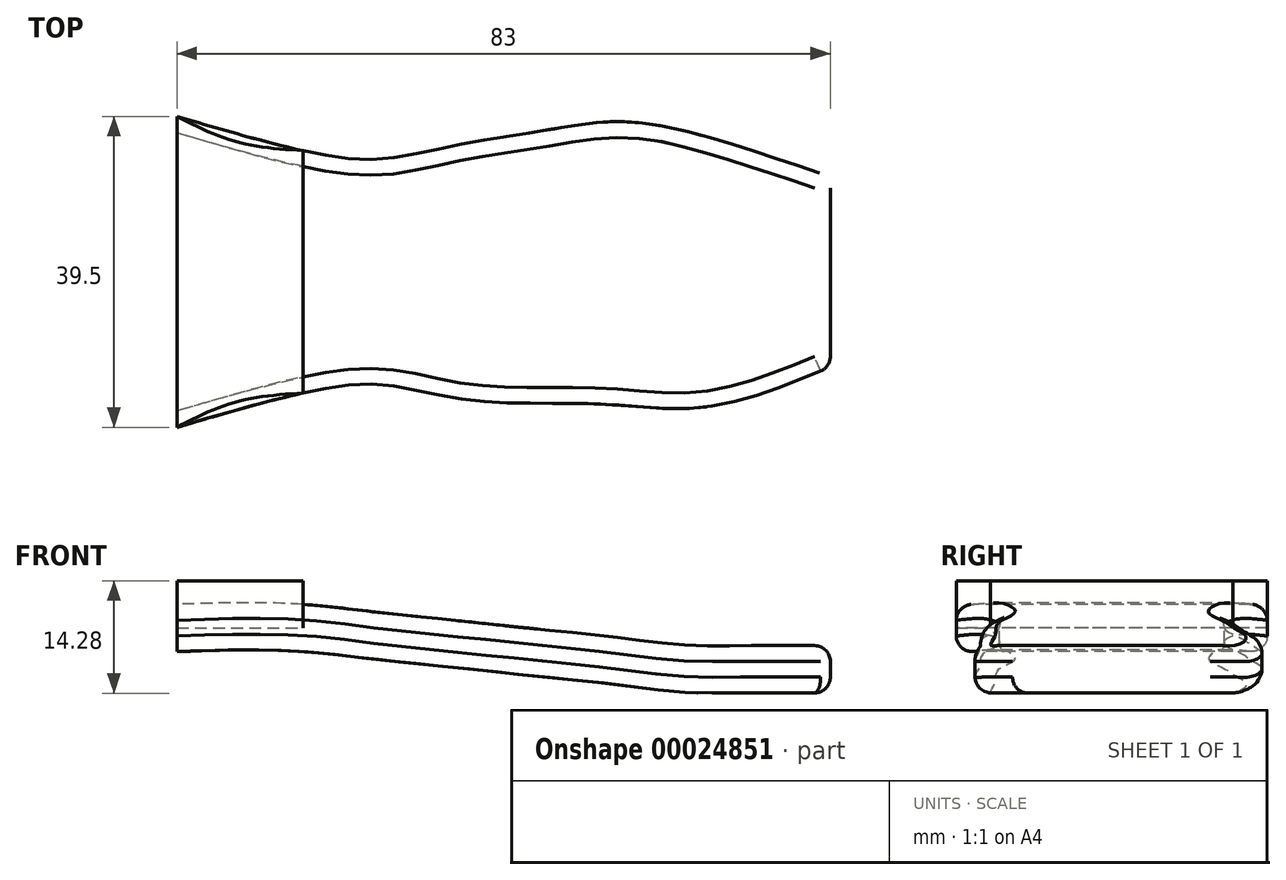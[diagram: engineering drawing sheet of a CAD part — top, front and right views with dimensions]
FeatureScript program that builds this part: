
annotation { "Feature Type Name" : "Feature", "Feature Type Description" : "" }
export const myFeature = defineFeature(function(context is Context, id is Id, definition is map)
    precondition{}
    {
        {
            var Q0;
            Q0=qCreatedBy(makeId("Top.planeOp"),FACE);
            var sketch = newSketch(context, id + "F0", { "sketchPlane" : qUnion([Q0])});
            skFitSpline(sketch, "E0", {"points": [v(0, 19.75) * mm, v(7.58, 16.5) * mm, v(16, 15.4) * mm], "startDerivative": vector(14.91, -7.63) * mm, "endDerivative": vector(17.08, -1.1) * mm});
            skFitSpline(sketch, "E1.MirrorCS", {"points": [v(0, -19.75) * mm, v(7.58, -16.5) * mm, v(16, -15.4) * mm], "startDerivative": vector(14.91, 7.63) * mm, "endDerivative": vector(17.08, 1.1) * mm});
            skLineSegment(sketch, "E2", {"start": v(0, 19.75) * mm, "end": v(0, -19.75) * mm});
            skLineSegment(sketch, "E3", {"start": v(16, 15.4) * mm, "end": v(16, -15.4) * mm});
            skSolve(sketch);
        }
        {
            var Q0;
            Q0=makeQuery(id+"F0.imprint","IMPRINT",FACE,{"disambiguationData":[TD([[makeQuery(id+"F0.imprint","IMPRINT",EDGE,{"derivedFrom":sQuery(id+"F0.wireOp",EDGE,"E0")}),-1.0]])]});
            extrude(context, id + "F1", {"entities" : qUnion([Q0]), "depth" : 6 * mm});
        }
        {
            var Q0;
            Q0=makeQuery(id+"F1.opExtrude","SWEPT_FACE",FACE,{"disambiguationData":[OSD([sQuery(id+"F0.wireOp",EDGE,"E3")])]});
            cPlane(context, id + "F2", {"entities" : qUnion([Q0]), "cplaneType" : CPlaneType.OFFSET, "offset" : 0 * mm, "width" : 152.4 * mm, "height" : 152.4 * mm});
        }
        {
            var Q0;
            Q0=qCreatedBy(id+"F2.planeOp",FACE);
            cPlane(context, id + "F3", {"entities" : qUnion([Q0]), "cplaneType" : CPlaneType.OFFSET, "offset" : 9.5 * mm, "width" : 152.4 * mm, "height" : 152.4 * mm});
        }
        {
            var Q0;
            Q0=qCreatedBy(id+"F3.planeOp",FACE);
            cPlane(context, id + "F4", {"entities" : qUnion([Q0]), "cplaneType" : CPlaneType.OFFSET, "offset" : 9.5 * mm, "width" : 152.4 * mm, "height" : 152.4 * mm});
        }
        {
            var Q0;
            Q0=qCreatedBy(id+"F3.planeOp",FACE);
            var sketch = newSketch(context, id + "F5", { "sketchPlane" : qUnion([Q0])});
            skLineSegment(sketch, "E4.rect.bottom", {"start": v(-14.3, 2) * mm, "end": v(14.3, 2) * mm});
            skLineSegment(sketch, "E4.rect.top", {"start": v(-14.3, -4) * mm, "end": v(14.3, -4) * mm});
            skLineSegment(sketch, "E4.rect.left", {"start": v(-14.3, 2) * mm, "end": v(-14.3, -4) * mm});
            skLineSegment(sketch, "E4.rect.right", {"start": v(14.3, 2) * mm, "end": v(14.3, -4) * mm});
            skPoint(sketch, "E4.rect.middle", {"position": v(0, -1) * mm});
            skSolve(sketch);
        }
        {
            var Q0;
            Q0=qCreatedBy(id+"F4.planeOp",FACE);
            var sketch = newSketch(context, id + "F6", { "sketchPlane" : qUnion([Q0])});
            skLineSegment(sketch, "E5.rect.bottom", {"start": v(16, 1) * mm, "end": v(-16, 1) * mm});
            skLineSegment(sketch, "E5.rect.top", {"start": v(16, -5) * mm, "end": v(-16, -5) * mm});
            skLineSegment(sketch, "E5.rect.left", {"start": v(16, 1) * mm, "end": v(16, -5) * mm});
            skLineSegment(sketch, "E5.rect.right", {"start": v(-16, 1) * mm, "end": v(-16, -5) * mm});
            skSolve(sketch);
        }
        {
            var Q0;
            Q0=qCreatedBy(id+"F4.planeOp",FACE);
            cPlane(context, id + "F7", {"entities" : qUnion([Q0]), "cplaneType" : CPlaneType.OFFSET, "offset" : 12 * mm, "width" : 152.4 * mm, "height" : 152.4 * mm});
        }
        {
            var Q0;
            Q0=qCreatedBy(id+"F7.planeOp",FACE);
            cPlane(context, id + "F8", {"entities" : qUnion([Q0]), "cplaneType" : CPlaneType.OFFSET, "offset" : 8.5 * mm, "width" : 152.4 * mm, "height" : 152.4 * mm});
        }
        {
            var Q0;
            Q0=qCreatedBy(id+"F8.planeOp",FACE);
            cPlane(context, id + "F9", {"entities" : qUnion([Q0]), "cplaneType" : CPlaneType.OFFSET, "offset" : 10.5 * mm, "width" : 152.4 * mm, "height" : 152.4 * mm});
        }
        {
            var Q0;
            Q0=qCreatedBy(id+"F9.planeOp",FACE);
            cPlane(context, id + "F10", {"entities" : qUnion([Q0]), "cplaneType" : CPlaneType.OFFSET, "offset" : 4 * mm, "width" : 152.4 * mm, "height" : 152.4 * mm});
        }
        {
            var Q0;
            Q0=qCreatedBy(id+"F10.planeOp",FACE);
            cPlane(context, id + "F11", {"entities" : qUnion([Q0]), "cplaneType" : CPlaneType.OFFSET, "offset" : 13 * mm, "width" : 152.4 * mm, "height" : 152.4 * mm});
        }
        {
            var Q0;
            Q0=qCreatedBy(id+"F7.planeOp",FACE);
            var sketch = newSketch(context, id + "F12", { "sketchPlane" : qUnion([Q0])});
            skPoint(sketch, "E6.rect.middle", {"position": v(0, -3.26) * mm});
            skLineSegment(sketch, "E7", {"start": v(-16.7, -0.26) * mm, "end": v(18, -0.26) * mm});
            skLineSegment(sketch, "E8.MirrorCS", {"start": v(-16.7, -6.26) * mm, "end": v(18, -6.26) * mm});
            skLineSegment(sketch, "E9", {"start": v(-16.7, -0.26) * mm, "end": v(-16.7, -6.26) * mm});
            skLineSegment(sketch, "E10", {"start": v(18, -0.26) * mm, "end": v(18, -6.26) * mm});
            skSolve(sketch);
        }
        {
            var Q0;
            Q0=qCreatedBy(id+"F8.planeOp",FACE);
            var sketch = newSketch(context, id + "F13", { "sketchPlane" : qUnion([Q0])});
            skLineSegment(sketch, "E11", {"start": v(19.08, -1.15) * mm, "end": v(-16.9, -1.15) * mm});
            skLineSegment(sketch, "E12.MirrorCS", {"start": v(19.08, -7.15) * mm, "end": v(-16.9, -7.15) * mm});
            skLineSegment(sketch, "E13", {"start": v(-16.9, -7.15) * mm, "end": v(-16.9, -1.15) * mm});
            skLineSegment(sketch, "E14", {"start": v(19.08, -1.15) * mm, "end": v(19.08, -7.15) * mm});
            skSolve(sketch);
        }
        {
            var Q0;
            Q0=qCreatedBy(id+"F9.planeOp",FACE);
            var sketch = newSketch(context, id + "F14", { "sketchPlane" : qUnion([Q0])});
            skLineSegment(sketch, "E15", {"start": v(-17.3, -2.25) * mm, "end": v(17.5, -2.25) * mm});
            skLineSegment(sketch, "E16.MirrorCS", {"start": v(-17.3, -8.25) * mm, "end": v(17.5, -8.25) * mm});
            skLineSegment(sketch, "E17", {"start": v(17.5, -2.25) * mm, "end": v(17.5, -8.25) * mm});
            skLineSegment(sketch, "E18", {"start": v(-17.3, -2.25) * mm, "end": v(-17.3, -8.25) * mm});
            skSolve(sketch);
        }
        {
            var Q0;
            Q0=qCreatedBy(id+"F10.planeOp",FACE);
            var sketch = newSketch(context, id + "F15", { "sketchPlane" : qUnion([Q0])});
            skLineSegment(sketch, "E19", {"start": v(-16.68, -2.25) * mm, "end": v(16.35, -2.25) * mm});
            skLineSegment(sketch, "E20.MirrorCS", {"start": v(-16.68, -8.25) * mm, "end": v(16.35, -8.25) * mm});
            skLineSegment(sketch, "E21", {"start": v(16.35, -2.25) * mm, "end": v(16.35, -8.25) * mm});
            skLineSegment(sketch, "E22", {"start": v(-16.68, -2.25) * mm, "end": v(-16.68, -8.25) * mm});
            skSolve(sketch);
        }
        {
            var Q0;
            Q0=qCreatedBy(id+"F11.planeOp",FACE);
            var sketch = newSketch(context, id + "F16", { "sketchPlane" : qUnion([Q0])});
            skLineSegment(sketch, "E23.rect.bottom", {"start": v(-12.09, -2.25) * mm, "end": v(12.09, -2.25) * mm});
            skLineSegment(sketch, "E23.rect.top", {"start": v(-12.09, -8.25) * mm, "end": v(12.09, -8.25) * mm});
            skLineSegment(sketch, "E23.rect.left", {"start": v(-12.09, -2.25) * mm, "end": v(-12.09, -8.25) * mm});
            skLineSegment(sketch, "E23.rect.right", {"start": v(12.09, -2.25) * mm, "end": v(12.09, -8.25) * mm});
            skSolve(sketch);
        }
        {
            var Q0;
            Q0=qCreatedBy(makeId("Right.planeOp"),FACE);
            var sketch = newSketch(context, id + "F17", { "sketchPlane" : qUnion([Q0])});
            skLineSegment(sketch, "E24.rect.bottom", {"start": v(19.75, 3) * mm, "end": v(-19.75, 3) * mm});
            skLineSegment(sketch, "E24.rect.top", {"start": v(19.75, -3) * mm, "end": v(-19.75, -3) * mm});
            skLineSegment(sketch, "E24.rect.left", {"start": v(19.75, 3) * mm, "end": v(19.75, -3) * mm});
            skLineSegment(sketch, "E24.rect.right", {"start": v(-19.75, 3) * mm, "end": v(-19.75, -3) * mm});
            skPoint(sketch, "E24.rect.middle", {"position": v(0, 0) * mm});
            skSolve(sketch);
        }
        {
            var Q0;
            Q0=qCreatedBy(id+"F2.planeOp",FACE);
            var sketch = newSketch(context, id + "F18", { "sketchPlane" : qUnion([Q0])});
            skLineSegment(sketch, "E25.rect.bottom", {"start": v(-15.4, 3) * mm, "end": v(15.4, 3) * mm});
            skLineSegment(sketch, "E25.rect.top", {"start": v(-15.4, -3) * mm, "end": v(15.4, -3) * mm});
            skLineSegment(sketch, "E25.rect.left", {"start": v(-15.4, 3) * mm, "end": v(-15.4, -3) * mm});
            skLineSegment(sketch, "E25.rect.right", {"start": v(15.4, 3) * mm, "end": v(15.4, -3) * mm});
            skPoint(sketch, "E25.rect.middle", {"position": v(0, 0) * mm});
            skSolve(sketch);
        }
        {
            var Q0;
            Q0=makeQuery(id+"F17.imprint","IMPRINT",FACE,{"disambiguationData":[TD([[makeQuery(id+"F17.imprint","IMPRINT",EDGE,{"derivedFrom":sQuery(id+"F17.wireOp",EDGE,"E24.rect.bottom")}),1.0]])]});
            var Q1;
            Q1=makeQuery(id+"F18.imprint","IMPRINT",FACE,{"disambiguationData":[TD([[makeQuery(id+"F18.imprint","IMPRINT",EDGE,{"derivedFrom":sQuery(id+"F18.wireOp",EDGE,"E25.rect.bottom")}),-1.0]])]});
            var Q2;
            Q2=makeQuery(id+"F5.imprint","IMPRINT",FACE,{"disambiguationData":[TD([[makeQuery(id+"F5.imprint","IMPRINT",EDGE,{"derivedFrom":sQuery(id+"F5.wireOp",EDGE,"E4.rect.bottom")}),-1.0]])]});
            var Q3;
            Q3=makeQuery(id+"F6.imprint","IMPRINT",FACE,{"disambiguationData":[TD([[makeQuery(id+"F6.imprint","IMPRINT",EDGE,{"derivedFrom":sQuery(id+"F6.wireOp",EDGE,"E5.rect.bottom")}),1.0]])]});
            var Q4;
            Q4=makeQuery(id+"F12.imprint","IMPRINT",FACE,{"disambiguationData":[TD([[makeQuery(id+"F12.imprint","IMPRINT",EDGE,{"derivedFrom":sQuery(id+"F12.wireOp",EDGE,"E7")}),-1.0]])]});
            var Q5;
            Q5=makeQuery(id+"F13.imprint","IMPRINT",FACE,{"disambiguationData":[TD([[makeQuery(id+"F13.imprint","IMPRINT",EDGE,{"derivedFrom":sQuery(id+"F13.wireOp",EDGE,"E11")}),1.0]])]});
            var Q6;
            Q6=makeQuery(id+"F14.imprint","IMPRINT",FACE,{"disambiguationData":[TD([[makeQuery(id+"F14.imprint","IMPRINT",EDGE,{"derivedFrom":sQuery(id+"F14.wireOp",EDGE,"E15")}),-1.0]])]});
            var Q7;
            Q7=makeQuery(id+"F15.imprint","IMPRINT",FACE,{"disambiguationData":[TD([[makeQuery(id+"F15.imprint","IMPRINT",EDGE,{"derivedFrom":sQuery(id+"F15.wireOp",EDGE,"E19")}),-1.0]])]});
            var Q8;
            Q8=makeQuery(id+"F16.imprint","IMPRINT",FACE,{"disambiguationData":[TD([[makeQuery(id+"F16.imprint","IMPRINT",EDGE,{"derivedFrom":sQuery(id+"F16.wireOp",EDGE,"E23.rect.bottom")}),-1.0]])]});
            loft(context, id + "F19", {"sheetProfilesArray" : [{ "sheetProfileEntities" : qUnion([Q0]) }, { "sheetProfileEntities" : qUnion([Q1]) }, { "sheetProfileEntities" : qUnion([Q2]) }, { "sheetProfileEntities" : qUnion([Q3]) }, { "sheetProfileEntities" : qUnion([Q4]) }, { "sheetProfileEntities" : qUnion([Q5]) }, { "sheetProfileEntities" : qUnion([Q6]) }, { "sheetProfileEntities" : qUnion([Q7]) }, { "sheetProfileEntities" : qUnion([Q8]) }]});
        }
        {
            var Q0;
            Q0=makeQuery(id+"F19.opLoft","SWEPT_EDGE",EDGE,{"disambiguationData":[OSD([sQuery(id+"F17.wireOp",EDGE,"E24.rect.bottom"),sQuery(id+"F17.wireOp",EDGE,"E24.rect.right"),sQuery(id+"F18.wireOp",EDGE,"E25.rect.bottom"),sQuery(id+"F18.wireOp",EDGE,"E25.rect.left")])]});
            var Q1;
            Q1=makeQuery(id+"F19.opLoft","SWEPT_EDGE",EDGE,{"disambiguationData":[OSD([sQuery(id+"F17.wireOp",EDGE,"E24.rect.top"),sQuery(id+"F17.wireOp",EDGE,"E24.rect.right"),sQuery(id+"F18.wireOp",EDGE,"E25.rect.top"),sQuery(id+"F18.wireOp",EDGE,"E25.rect.left")])]});
            var Q2;
            Q2=makeQuery(id+"F19.opLoft","SWEPT_EDGE",EDGE,{"disambiguationData":[OSD([sQuery(id+"F15.wireOp",EDGE,"E19"),sQuery(id+"F15.wireOp",EDGE,"E21"),sQuery(id+"F16.wireOp",EDGE,"E23.rect.bottom"),sQuery(id+"F16.wireOp",EDGE,"E23.rect.right")])]});
            var Q3;
            Q3=makeQuery(id+"F19.opLoft","SWEPT_EDGE",EDGE,{"disambiguationData":[OSD([sQuery(id+"F15.wireOp",EDGE,"E20.MirrorCS"),sQuery(id+"F15.wireOp",EDGE,"E21"),sQuery(id+"F16.wireOp",EDGE,"E23.rect.top"),sQuery(id+"F16.wireOp",EDGE,"E23.rect.right")])]});
            var Q4;
            Q4=makeQuery(id+"F19.opLoft","MID_CAP_EDGE",EDGE,{"disambiguationData":[OSD([sQuery(id+"F16.wireOp",EDGE,"E23.rect.bottom"),sQuery(id+"F16.wireOp",EDGE,"E23.rect.top"),sQuery(id+"F16.wireOp",EDGE,"E23.rect.right")])],"capPos":8.0});
            var Q5;
            Q5=makeQuery(id+"F19.opLoft","MID_CAP_EDGE",EDGE,{"disambiguationData":[OSD([sQuery(id+"F16.wireOp",EDGE,"E23.rect.bottom"),sQuery(id+"F16.wireOp",EDGE,"E23.rect.left"),sQuery(id+"F16.wireOp",EDGE,"E23.rect.right")])],"capPos":8.0});
            var Q6;
            Q6=makeQuery(id+"F19.opLoft","MID_CAP_EDGE",EDGE,{"disambiguationData":[OSD([sQuery(id+"F16.wireOp",EDGE,"E23.rect.top"),sQuery(id+"F16.wireOp",EDGE,"E23.rect.left"),sQuery(id+"F16.wireOp",EDGE,"E23.rect.right")])],"capPos":8.0});
            var Q7;
            Q7=makeQuery(id+"F19.opLoft","MID_CAP_EDGE",EDGE,{"disambiguationData":[OSD([sQuery(id+"F16.wireOp",EDGE,"E23.rect.bottom"),sQuery(id+"F16.wireOp",EDGE,"E23.rect.top"),sQuery(id+"F16.wireOp",EDGE,"E23.rect.left")])],"capPos":8.0});
            fillet(context, id + "F20", {"entities" : qUnion([Q0, Q1, Q2, Q3, Q4, Q5, Q6, Q7]), "radius" : 2 * mm, "tangentPropagation" : true, "allowEdgeOverflow" : false});
        }
    });
